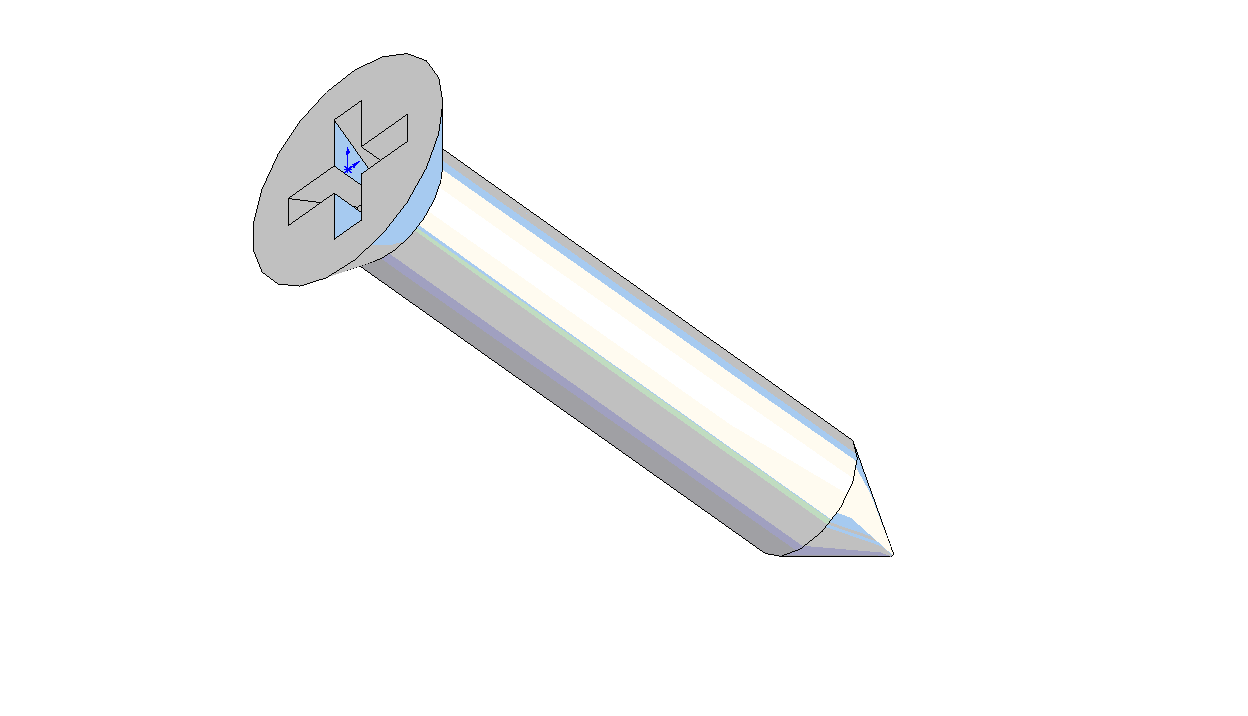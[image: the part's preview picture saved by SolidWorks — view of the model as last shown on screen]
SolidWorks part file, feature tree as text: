
SOLIDWORKS PART (.sldprt)
format: sldprt  version: not decoded by parser v0  size: 159,232 bytes
history: native  units: mm
features: plane x3, sketch x3, material x1, revolve x1, extrude x1, cut_extrude x1, chamfer x1 (+8 scaffold rows collapsed)
feature tree (19):
  scaffold x8  (default folders/planes/origin — collapsed)
  material  "Matériau <non spécifié>"
  plane  "Plan de face"
  plane  "Plan de dessus"
  plane  "Plan de droite"
  sketch  "Esquisse1"  dims[c1.D1=~11.352469mm c2.D1=135.0deg]
  revolve  "Révolution2"  Angle=360deg
  sketch  "Esquisse3"  dims[D1=~1.457329mm]
  extrude  "Extrusion1"  Depth=16mm
  sketch  "Esquisse2"  dims[D1=0.4mm D2=0.4mm]
  cut_extrude  "Enlèv. mat.-Extru.2"  Depth=1.2mm
  chamfer  "Chanfrein1"  Distance=1.45mm Angle=60deg
decode coverage: 7 of 7 modeling features carry decoded parameters
note: ~ marks probable driven/reference dimensions
note: suppression state not decoded; provenance and decode notes live in map.json
